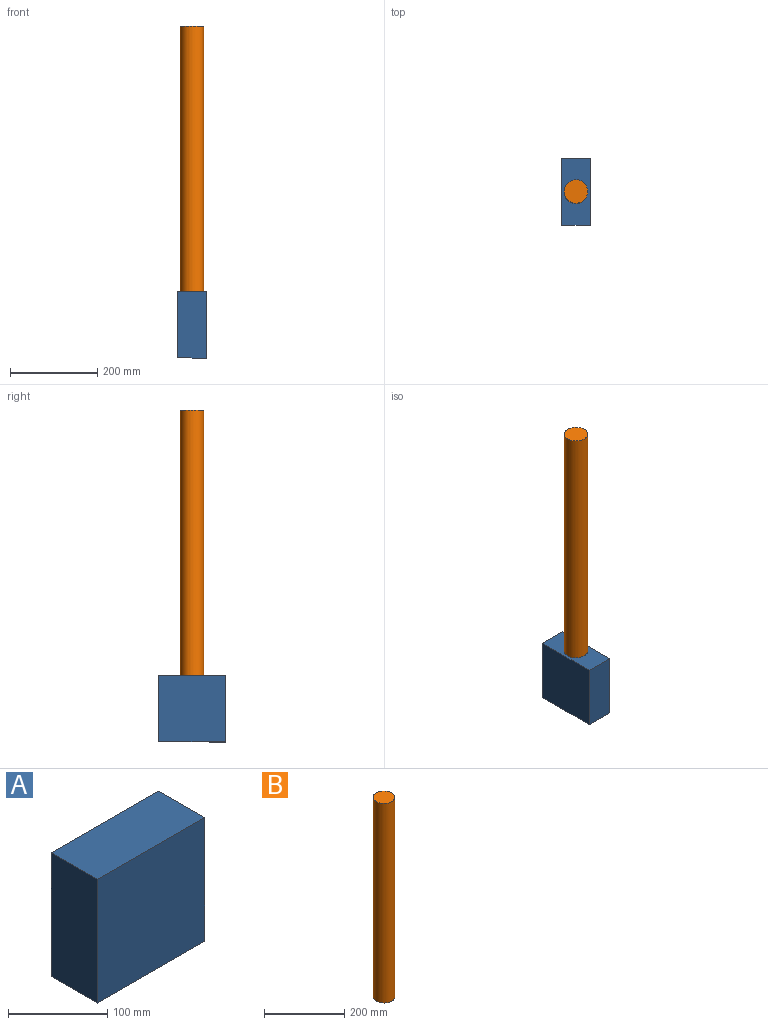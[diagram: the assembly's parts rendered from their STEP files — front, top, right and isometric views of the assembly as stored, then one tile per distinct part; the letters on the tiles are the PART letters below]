
ASSEMBLY  parts=2 mates=1
PART A: 6 faces, bbox 152.5x65.6x152.4 mm
  f0: plane 152.48x152.4mm, normal (0,-1,0), area 23238.5mm2, adj f1,f3,f4,f5
  f1: plane 152.4x65.56mm, normal (1,0,0), area 9990.8mm2, adj f0,f2,f3,f4
  f2: plane 152.48x152.4mm, normal (0,1,0), area 23238.5mm2, adj f1,f3,f4,f5
  f3: plane 152.48x65.56mm, normal (0,0,-1), area 9996.3mm2, adj f0,f1,f2,f5
  f4: plane 152.48x65.56mm, normal (0,0,1), area 9996.3mm2, adj f0,f1,f2,f5
  f5: plane 152.4x65.56mm, normal (-1,0,0), area 9990.8mm2, adj f0,f2,f3,f4
PART B: 3 faces, bbox 54.1x54.1x609.6 mm
  f0: cylinder r=27.03mm len=609.6mm, axis (0,0,-1), area 103539.8mm2, adj f1,f2
  f1: plane 54.06x54.06mm, normal (0,0,1), area 2295.7mm2, adj f0
  f2: plane 54.06x54.06mm, normal (0,0,-1), area 2295.7mm2, adj f0
PLACE A rot(axis=(0.71,-0.71,0),180deg) t=(24.24,65.01,-152.4)mm
PLACE B at identity
MATE fastened A.f3 <-> B.f0  axis (0,0,1) through (41.67,78.39,0)mm
